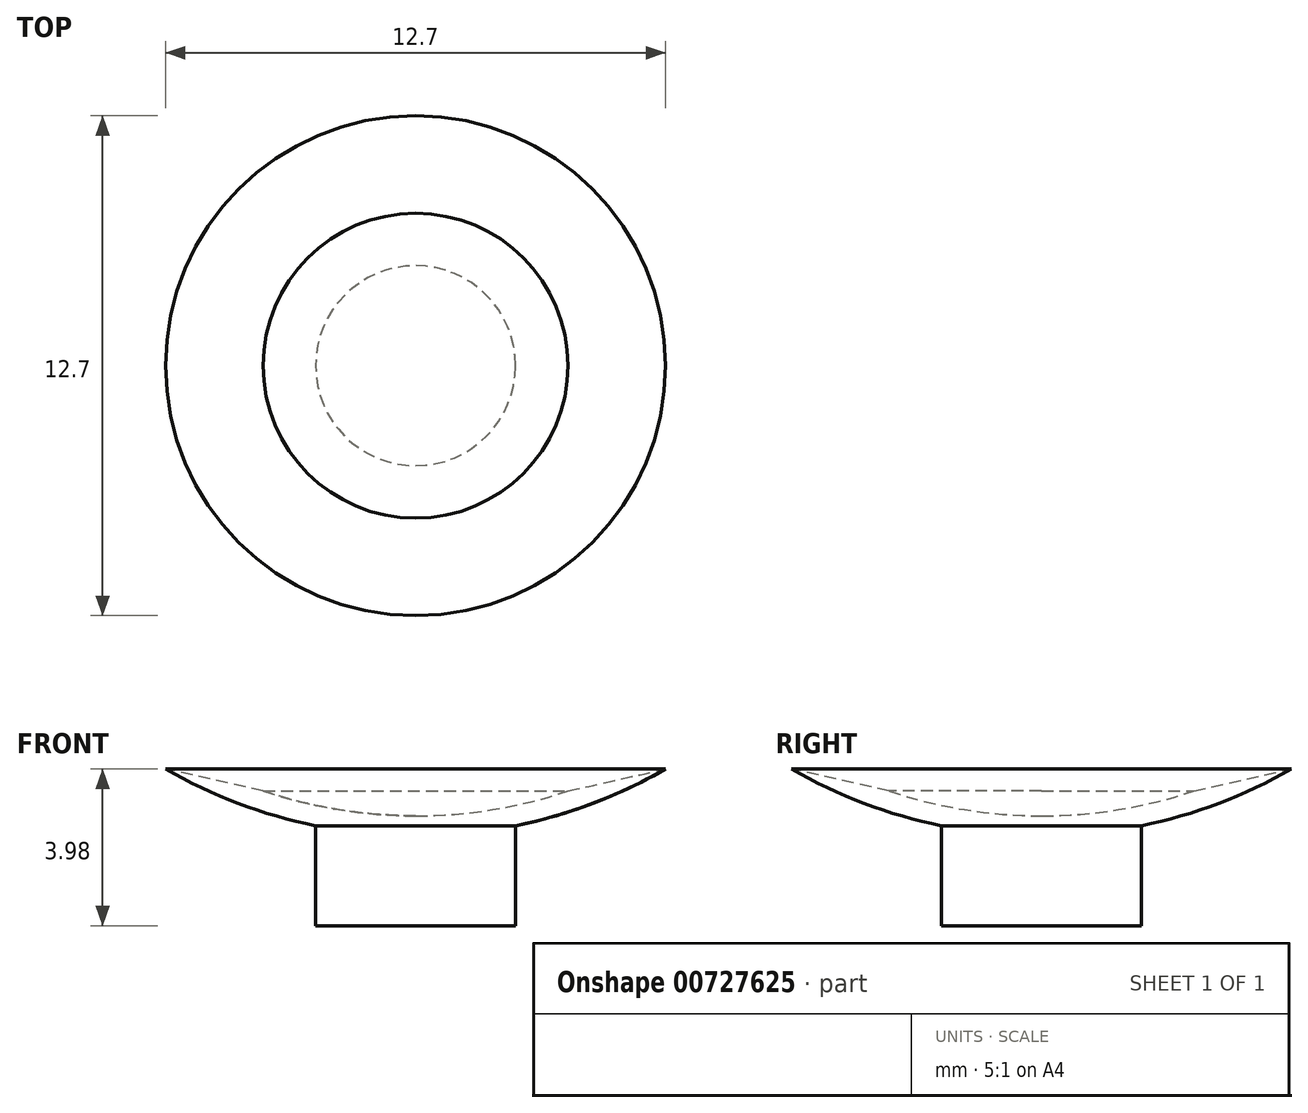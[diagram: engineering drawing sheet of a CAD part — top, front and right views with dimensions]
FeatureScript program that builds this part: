
annotation { "Feature Type Name" : "Feature", "Feature Type Description" : "" }
export const myFeature = defineFeature(function(context is Context, id is Id, definition is map)
    precondition{}
    {
        {
            var Q0;
            Q0=qCreatedBy(makeId("Front.planeOp"),FACE);
            var sketch = newSketch(context, id + "F0", { "sketchPlane" : qUnion([Q0])});
            skLineSegment(sketch, "E0", {"start": v(0, 0) * mm, "end": v(2.54, 0) * mm});
            skLineSegment(sketch, "E1", {"start": v(2.54, 0) * mm, "end": v(2.54, 2.54) * mm});
            skArc(sketch, "E2", {"start": v(0, 2.8) * mm, "mid": v(1.96, 2.95) * mm, "end": v(3.87, 3.42) * mm});
            skLineSegment(sketch, "E3", {"start": v(0, 2.8) * mm, "end": v(0, 0) * mm});
            skArc(sketch, "E4", {"start": v(2.54, 2.54) * mm, "mid": v(4.5, 3.1) * mm, "end": v(6.35, 3.98) * mm});
            skLineSegment(sketch, "E5", {"start": v(3.87, 3.42) * mm, "end": v(6.35, 3.98) * mm});
            skSolve(sketch);
        }
        {
            var Q0;
            Q0 = qSketchRegion(id + "F0", true);
            var Q1;
            Q1=makeQuery(id+"F0.imprint","IMPRINT",FACE,{"disambiguationData":[TD([[makeQuery(id+"F0.imprint","IMPRINT",EDGE,{"derivedFrom":sQuery(id+"F0.wireOp",EDGE,"E0")}),1.0]])]});
            var Q2;
            Q2=sQuery(id+"F0.wireOp",EDGE,"E3");
            revolve(context, id + "F1", {"surfaceOperationType" : NewSurfaceOperationType.NEW, "entities" : qUnion([Q0, Q1]), "axis" : qUnion([Q2]), "revolveType" : RevolveType.FULL});
        }
    });
